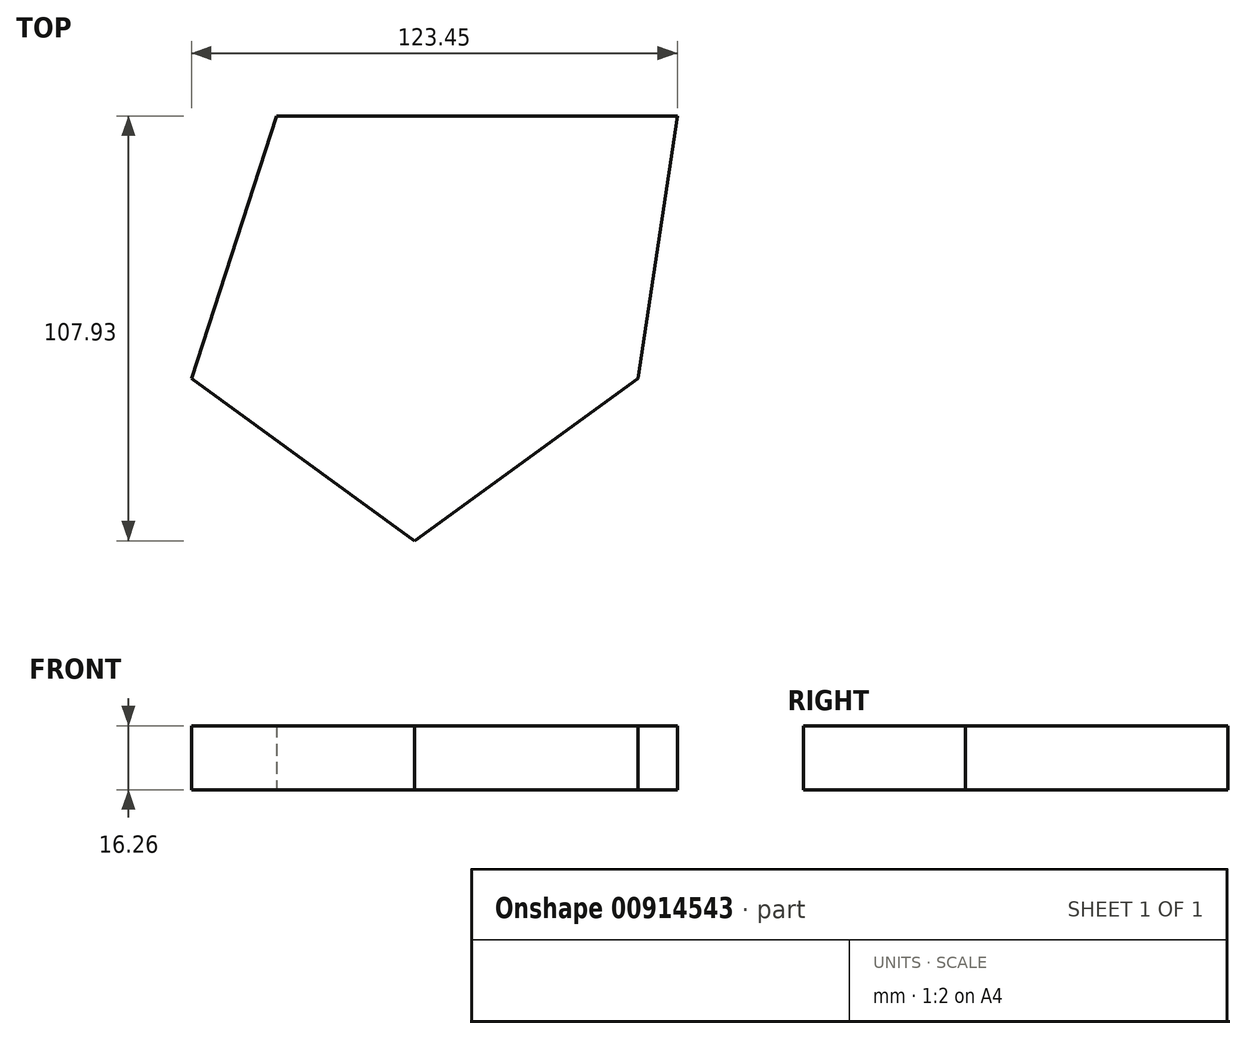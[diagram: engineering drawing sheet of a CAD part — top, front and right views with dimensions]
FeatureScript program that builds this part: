
annotation { "Feature Type Name" : "Feature", "Feature Type Description" : "" }
export const myFeature = defineFeature(function(context is Context, id is Id, definition is map)
    precondition{}
    {
        {
            var Q0;
            Q0=qCreatedBy(makeId("Top.planeOp"),FACE);
            var sketch = newSketch(context, id + "F0", { "sketchPlane" : qUnion([Q0])});
            skCircle(sketch, "E0.cCircle", {"center": v(0, 0) * mm, "radius": 48.27 * mm, "construction": true});
            skLineSegment(sketch, "E0.0", {"start": v(-35.07, 48.27) * mm, "end": v(35.07, 48.27) * mm});
            skLineSegment(sketch, "E0.2", {"start": v(56.74, -18.44) * mm, "end": v(0, -59.66) * mm});
            skLineSegment(sketch, "E0.3", {"start": v(0, -59.66) * mm, "end": v(-56.74, -18.44) * mm});
            skLineSegment(sketch, "E0.4", {"start": v(-56.74, -18.44) * mm, "end": v(-35.07, 48.27) * mm});
            skPoint(sketch, "E0.0.midPoint", {"position": v(0, 48.27) * mm});
            skLineSegment(sketch, "E1", {"start": v(35.07, 48.27) * mm, "end": v(66.71, 48.27) * mm});
            skLineSegment(sketch, "E2", {"start": v(66.71, 48.27) * mm, "end": v(56.74, -18.44) * mm});
            skSolve(sketch);
        }
        {
            var Q0;
            Q0 = qSketchRegion(id + "F0", true);
            extrude(context, id + "F1", {"entities" : qUnion([Q0]), "depth" : 16.26 * mm, "offsetDistance" : 25.4 * mm});
        }
    });
